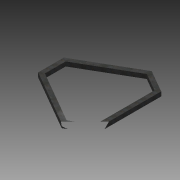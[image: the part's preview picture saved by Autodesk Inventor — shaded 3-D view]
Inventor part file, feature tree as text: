
AUTODESK INVENTOR PART (.ipt)
format: ipt  version: 2015 SP1 (Build 190203100, 203)  size: 88,064 bytes
history: native  units: in
note: dims shown in document units (in); Inventor stores cm internally (conversion verified against a paired STEP export)
features: extrude x1, sketch x1
ambient origin geometry x8: Origin, YZ Plane, XZ Plane, XY Plane, X Axis, Y Axis, Z Axis, Center Point
bodies: Body1 (feature_tree)
feature tree (2):
  extrude  "Extrusion7"  Depth=2.0in TaperAngle=0.0deg
  sketch  "Sketch1"  dims[d48=2.0in d49=2.0in d50=0.0in]
